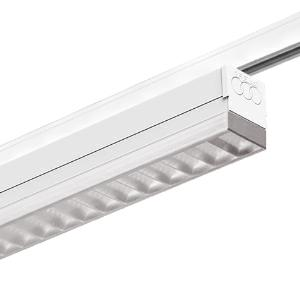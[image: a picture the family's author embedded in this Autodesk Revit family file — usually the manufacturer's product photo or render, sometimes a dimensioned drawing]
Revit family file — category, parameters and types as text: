
# Revit family: 3f_filippi_-_3f_zeta_track_dr_ugr_3f_filippi_-_47170_-_3f_zeta_tk_dr_ugr_1x30-940_dali_l1783
name_source: partatom
category: Lighting Fixtures
units: mm (PartAtom-declared; Revit-internal decimal feet)

## family parameters
Cut with Voids When Loaded = No
Host = Face
Light Source = No
Part Type = Normal
Room Calculation Point = No
Round Connector Dimension = Use Diameter
Shared = No

## types (1)
- 3F Filippi - 3F Zeta Track DR UGR (1 x LED, 2702 lm, 34 W, 4000 K)
    Apparent Load = 34 VA
    Approval mark = ENEC
    CIE Flux Codes = 69 97 100 100 100
    Color Rendering = 90
    Color Temperature = 4000 K
    Control Gear = Electronic transformer
    Default Elevation = 1800 mm
    Description = ILLUMINOTECHNICAL
Luminous efficiency 100% (DLOR 99%, ULOR 1%).
Initial luminous flux of the luminaire 2702 lm.
Controlled symmetric distribution.
Installation Interdistance Transv.D = 1.38 x hu - Long.D = 1.25 x hu.
Average luminance <1500 cd/m² for radial angles >65°.
Tabular UGR (CIE 117 - 4H-8H; S=0.25H; 70/50/20): RUG 15.7 - 17.1.
Beam angle: 87° - 91°.
Luminous efficacy 79 lm/W.
Lifetime (L93/B10): 30000 h. (tq+25°C)
Lifetime (L90/B10): 50000 h. (tq+25°C)
Lifetime (L85/B10): 80000 h. (tq+25°C)
Lifetime (L80/B10): 100000 h. (tq+25°C)
Sudden decreased luminous flux after 50000 hours: 0% (C0).
Photobiological safety in compliance with IEC/TR 62778: RG0 risk exempt, (IEC 62471).
In compliance with IEC/EN 62722-2-1 - IEC/EN 62717 standards.

SOURCE
Linear LED module 30W/940.
Energy efficiency class (UE 2019/2020 - UE 2019/2015): E.
CIE 13.3 Colour rendering index: CRI >90 (R9 >50%).
IES TM-30 Fidelity Index: Rf = 92 Rg = 101.
CCT nominal colour temperature 4000 K.
Colour initial tolerance (MacAdam): SDCM 3.

MECHANICAL
Housing in hot-galvanised steel, painted in white polyester, obtained through rolling process with adapters to busbar in white polycarbonate.
Light unit in hot-galvanised steel, painted in white polyester base with fixing springs and retractable safety hooks in stainless steel.
Rectangular transparent polycarbonate diffuser.
Semi-specular aluminium internal louvre with prismatic methacrylate (PMMA) filter above the louvre blades for complete shielding of the louvre compartment.
Supporting mechanical adapter.
End caps in white polycarbonate.
Luminaire with limited surface temperature. - D - (EN 60598-2-24)
Dimensions: 1783x62 mm, height 81 mm. Weight 4.69 kg.
IP40 protection degree.
Mechanical strength to impacts IK06 (1 joule).
Glow-wire test resistance 650°C.

ELECTRICAL
Halogen Free DALI-2 DATI (Parts 251, 252, 253), PUSH-DIM, electronic wiring 230V-50/60Hz, power factor 0.95 at full load, THD <25%, constant output current, SELV, class I, 1 driver, 1 DALI addresse.
Power of the luminaire 34 W.
CE - IEC 60598-1 - EN 60598-1.
SAFE FLICKER: PstLM=<1 and SVM=<0.4 (IEC TR 61547-1 and IEC TR 63158), to ensure a more comfortable and safe light.
Ambient temperature from 0°C to +25°C.
Temperature class T6 max 85°C.
Truck adapter, 6-way.
Relative humidity UR: <85%.

INSTALLATION
Track.
This product is suitable for installation on a 3-phase electrified busbar "Binario 3F".

APPLICATIONS
Environments: architectural, commercial, transit areas, cornices, boards.

LIGHT MANAGEMENT
Recommended minimum setting: 10%.
The luminaire, equipped with (DALI-2 DATI) driver, can be controlled manually with 3F Easy Dim technology or automatically/manually with wired or wireless DALI/D2D control systems.
The D2D driver guarantees interoperability with other devices with the same certification by making the following information available:
Device Data (Part 251), Energy Report (Part 252), Diagnosis & Maintenance (Part 253).
In electrical systems without a regulation system (manual or automatic) and DALI bus, a suitable jumper must be made on the DA-DA terminals of the appliance.

WARNING
Luminaire designed for disposal/recycling at end-of-life.
Replaceable (LED only) light source by a professional. Replaceable control gear by a professional.
    Height = 81 mm
    Lamp = 1 x LED
    Lamp Light Flux = 2702 lm
    Lamp Power = 34 W
    Lamp count = 1
    Length = 1783 mm
    Lifetime = 50000 h
    Luminous efficacy = 79 lm/W
    Manufacturer = 3F Filippi
    ModVariant = No
    Model = 3F Filippi - 47170 - 3F Zeta TK DR UGR 1x30-940 DALI L1783
    Mounting Place = Ceiling
    Mounting Type = Rail mounted
    Number of Poles = 1
    OnlyDefault = Yes
    Power Factor = 1
    Product Name = 3F Filippi - 3F Zeta Track DR UGR
    Product group = track mounted spotlight
    ProductGroupID = 12
    Protection Class = Protection class I
    Protection Degree = IP 40
    RLX_Detail_Level = 1
    RLX_Emergency_Light_Flux = 0 lm
    RLX_Emergency_Type = 0
    RLX_Emergency_Type_DB = No
    RlxData = <blob elided: 131757 chars, md5=65249848>
    Socket = socket
    Standby Power = 0 W
    System Light Flux = 2702 lm
    System Power = 34 W
    Type Comments = Product without accessories
    Type Image = 3ffilippi_3f_zeta_track_dr_ugr.jpg
    URL = http://relux.com
    VarID = ---
    Voltage = 0 V
    Weight = 0.00 kg
    Width = 62 mm  [stored 0.203412 ft]

note: [stored X ft] marks values corroborated as IEEE doubles in the binary element streams (Revit-internal decimal feet)

## geometry (parser evidence)
native form markers: Blend x4, Sweep x9
no freeform markers — native parametric forms only
